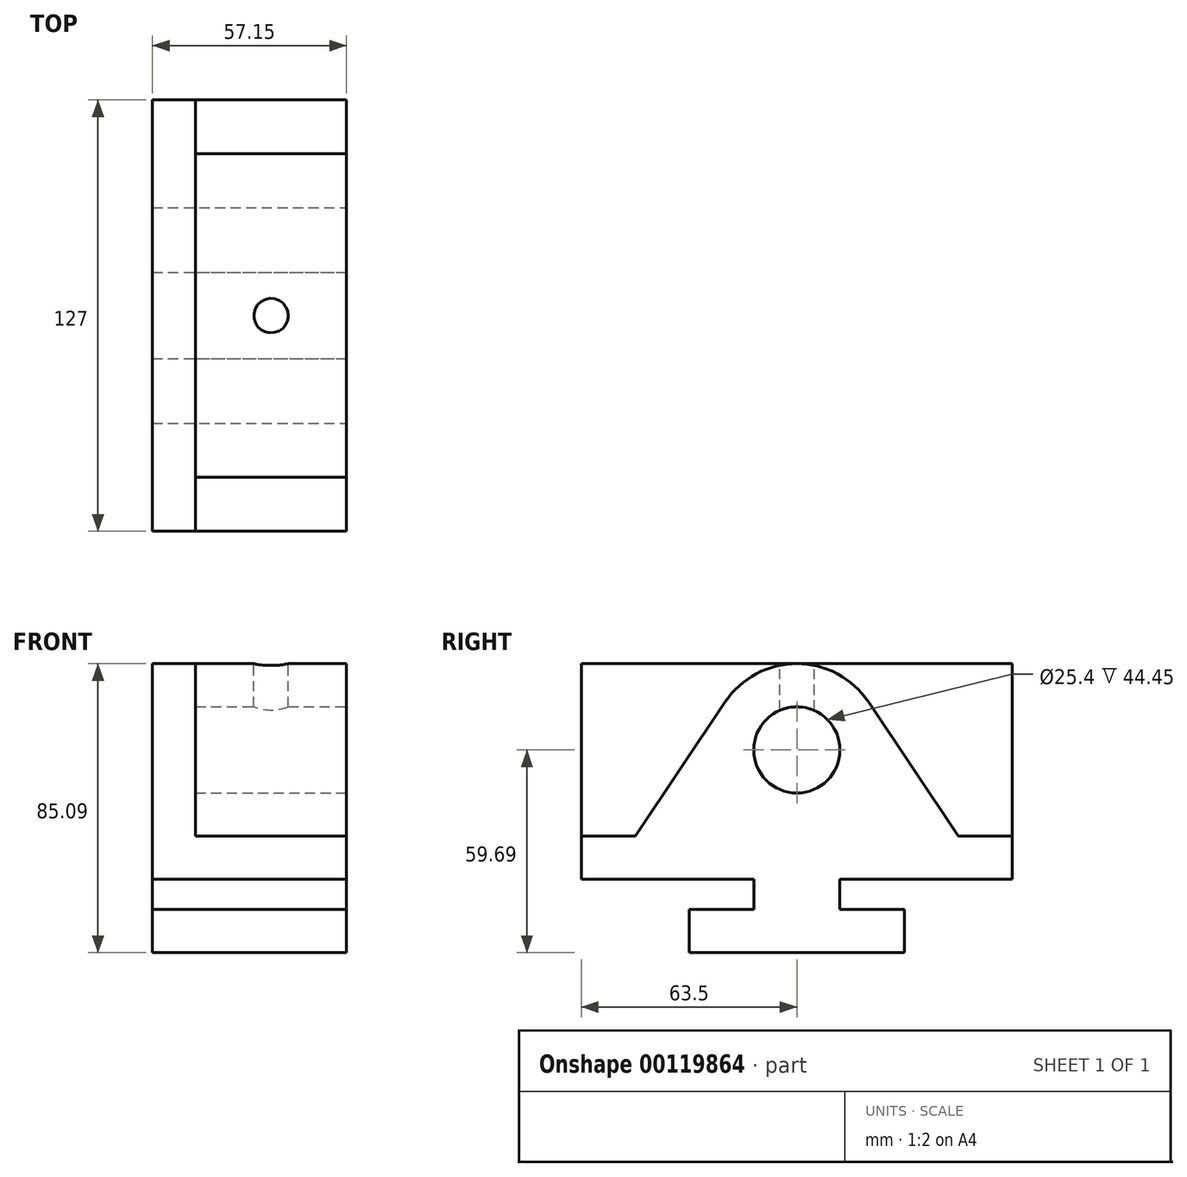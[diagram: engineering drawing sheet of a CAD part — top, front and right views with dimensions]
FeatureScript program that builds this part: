
annotation { "Feature Type Name" : "Feature", "Feature Type Description" : "" }
export const myFeature = defineFeature(function(context is Context, id is Id, definition is map)
    precondition{}
    {
        {
            var Q0;
            Q0=qCreatedBy(makeId("Right.planeOp"),FACE);
            var sketch = newSketch(context, id + "F0", { "sketchPlane" : qUnion([Q0])});
            skLineSegment(sketch, "E0", {"start": v(0, 0) * mm, "end": v(0, 12.7) * mm});
            skLineSegment(sketch, "E1", {"start": v(0, 12.7) * mm, "end": v(19.05, 12.7) * mm});
            skLineSegment(sketch, "E2", {"start": v(19.05, 12.7) * mm, "end": v(19.05, 21.59) * mm});
            skLineSegment(sketch, "E3", {"start": v(19.05, 21.6) * mm, "end": v(-31.75, 21.6) * mm});
            skLineSegment(sketch, "E4", {"start": v(-31.75, 21.59) * mm, "end": v(-31.75, 85.1) * mm});
            skLineSegment(sketch, "E5", {"start": v(-31.75, 85.1) * mm, "end": v(95.25, 85.1) * mm});
            skLineSegment(sketch, "E6", {"start": v(95.25, 85.1) * mm, "end": v(95.25, 21.6) * mm});
            skLineSegment(sketch, "E7", {"start": v(95.25, 21.6) * mm, "end": v(44.45, 21.6) * mm});
            skLineSegment(sketch, "E8", {"start": v(44.45, 21.59) * mm, "end": v(44.45, 12.7) * mm});
            skLineSegment(sketch, "E9", {"start": v(44.45, 12.7) * mm, "end": v(63.5, 12.7) * mm});
            skLineSegment(sketch, "E10", {"start": v(63.5, 12.7) * mm, "end": v(63.5, 0) * mm});
            skLineSegment(sketch, "E11", {"start": v(63.5, 0) * mm, "end": v(0, 0) * mm});
            skSolve(sketch);
        }
        {
            var Q0;
            Q0 = qSketchRegion(id + "F0", true);
            extrude(context, id + "F1", {"entities" : qUnion([Q0]), "oppositeDirection" : true, "depth" : 57.15 * mm});
        }
        {
            var Q0;
            Q0=makeQuery(id+"F1.opExtrude","CAP_FACE",FACE,{"disambiguationData":[OSD([sQuery(id+"F0.wireOp",EDGE,"E0"),sQuery(id+"F0.wireOp",EDGE,"E1"),sQuery(id+"F0.wireOp",EDGE,"E2"),sQuery(id+"F0.wireOp",EDGE,"E3"),sQuery(id+"F0.wireOp",EDGE,"E4"),sQuery(id+"F0.wireOp",EDGE,"E5"),sQuery(id+"F0.wireOp",EDGE,"E6"),sQuery(id+"F0.wireOp",EDGE,"E7"),sQuery(id+"F0.wireOp",EDGE,"E8"),sQuery(id+"F0.wireOp",EDGE,"E9"),sQuery(id+"F0.wireOp",EDGE,"E10"),sQuery(id+"F0.wireOp",EDGE,"E11")])],"isStart":true});
            var sketch = newSketch(context, id + "F2", { "sketchPlane" : qUnion([Q0])});
            skLineSegment(sketch, "E12", {"start": v(-31.75, 34.3) * mm, "end": v(-15.88, 34.3) * mm});
            skLineSegment(sketch, "E13", {"start": v(-15.88, 34.3) * mm, "end": v(10.66, 73.84) * mm});
            skLineSegment(sketch, "E14", {"start": v(95.25, 34.3) * mm, "end": v(79.38, 34.3) * mm});
            skLineSegment(sketch, "E15", {"start": v(79.38, 34.3) * mm, "end": v(52.84, 73.84) * mm});
            skArc(sketch, "E16", {"start": v(52.84, 73.84) * mm, "mid": v(31.75, 85.1) * mm, "end": v(10.66, 73.84) * mm});
            skSolve(sketch);
        }
        {
            var Q0;
            {var subQ6=sQuery(id+"F2.wireOp",EDGE,"E12");Q0=makeQuery(id+"F2.imprint","IMPRINT",FACE,{"disambiguationData":[TD([[makeQuery(id+"F2.imprint","IMPRINT",EDGE,{"derivedFrom":subQ6}),1.0]])]});}
            var Q1;
            {var subQ6=sQuery(id+"F2.wireOp",EDGE,"E14");Q1=makeQuery(id+"F2.imprint","IMPRINT",FACE,{"disambiguationData":[TD([[makeQuery(id+"F2.imprint","IMPRINT",EDGE,{"derivedFrom":subQ6}),-1.0]])]});}
            extrude(context, id + "F3", {"entities" : qUnion([Q0, Q1]), "operationType" : NewBodyOperationType.REMOVE, "oppositeDirection" : true, "depth" : 44.45 * mm});
        }
        {
            var Q0;
            {var subQ4=sQuery(id+"F2.wireOp",EDGE,"E12");Q0=makeQuery(id+"F2.imprint","IMPRINT",FACE,{"disambiguationData":[TD([[makeQuery(id+"F2.imprint","IMPRINT",EDGE,{"derivedFrom":subQ4}),-1.0]])]});}
            var sketch = newSketch(context, id + "F4", { "sketchPlane" : qUnion([Q0])});
            skCircle(sketch, "E17", {"center": v(31.75, 59.7) * mm, "radius": 12.7 * mm});
            skSolve(sketch);
        }
        {
            var Q0;
            Q0 = qSketchRegion(id + "F4", true);
            extrude(context, id + "F5", {"entities" : qUnion([Q0]), "operationType" : NewBodyOperationType.REMOVE, "oppositeDirection" : true, "depth" : 44.45 * mm});
        }
        {
            var Q0;
            Q0=qCreatedBy(makeId("Top.planeOp"),FACE);
            var sketch = newSketch(context, id + "F6", { "sketchPlane" : qUnion([Q0])});
            skLineSegment(sketch, "E18", {"start": v(0, 31.75) * mm, "end": v(-60.13, 31.75) * mm, "construction": true});
            skSolve(sketch);
        }
        {
            var Q0;
            Q0=makeQuery(id+"F1.opExtrude","SWEPT_FACE",FACE,{"disambiguationData":[OSD([sQuery(id+"F0.wireOp",EDGE,"E5")])]});
            cPlane(context, id + "F7", {"entities" : qUnion([Q0]), "cplaneType" : CPlaneType.OFFSET, "offset" : 0 * mm, "width" : 152.4 * mm, "height" : 152.4 * mm});
        }
        {
            var Q0;
            Q0=qCreatedBy(id+"F7.planeOp",FACE);
            var sketch = newSketch(context, id + "F8", { "sketchPlane" : qUnion([Q0])});
            skCircle(sketch, "E19", {"center": v(-22.23, 31.75) * mm, "radius": 5.08 * mm});
            skSolve(sketch);
        }
        {
            var Q0;
            Q0 = qSketchRegion(id + "F8", true);
            extrude(context, id + "F9", {"entities" : qUnion([Q0]), "operationType" : NewBodyOperationType.REMOVE, "oppositeDirection" : true, "depth" : 25.4 * mm});
        }
    });
